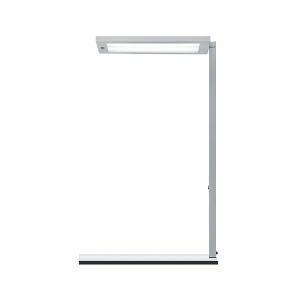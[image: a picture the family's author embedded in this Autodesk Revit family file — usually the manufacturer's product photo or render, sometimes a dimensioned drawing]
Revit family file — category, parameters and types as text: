
# Revit family: lavigo_core_-_dpt_9000_840_r_g1_srmet_00812479_ce18
name_source: partatom
category: Lighting Fixtures
units: mm (PartAtom-declared; Revit-internal decimal feet)

## family parameters
Cut with Voids When Loaded = No
Host = Face
Light Source = No
Part Type = Normal
Room Calculation Point = No
Round Connector Dimension = Use Diameter
Shared = No

## types (1)
- LAVIGO.core - DPT 9000/840/R/G1/SRMET (1 x LED, 8900 lm, 4000K)
    Apparent Load = 62 VA
    Approval mark = CE
    CIE Flux Codes = 59 88 97 35 100
    Color Rendering = 80-89
    Color Temperature = 4000K
    Control Gear = Electronic ballast
    Default Elevation = 1800 mm
    Description = DPT 9000/840/R/G1|Desk-mounted luminaire|light source: LED Cold white   |work equipment: Electronic ballast DALI|connected load: 220-240 V, 50/60 Hz|Power consumption: approx. 62 W|standby: approx. 0,30|power factor: approx. 0,959|luminous flux: 8900 lm|luminous efficacy: 143 lm/W|light distribution: Direct/indirect|direct ratio: approx. 35 %|color rendering index (CRI): >= 80|chromaticity tolerance:  3 SDCM|technology: Presence and daylight sensor control (PIR)|operation: Rocker switch|luminaire body|material: Steel/plastic|surface: Painted|colour: Silver metallic|lamp cover: Polycarbonate (PC), Clear|tubular section|material: Steel tube|surface: Painted|Form: Tubular section upright|colour of tubular section: Silver metallic|weight (net): approx. 8.3 kg|mains lead: 3.70 m Mains plug CEE 7/VII|Fastening: Socket, Table adaptor|decorative contrast side parts: Metallic silver|glare control: Prism aperture|luminance(L65): <= 4400 cd/m|unified glare rating(4H 8H): <=  16|special features: Luminaire head detachable, Direct and indirect light switchable together, Flicker-free, Integrated light and presence sensor PIR, Motion sensor time-out of 15mins~|
    Frequency = 50 Hz, 60 Hz
    Height = 36 mm
    Lamp = 1 x LED
    Lamp Light Flux = 8900 lm
    Lamp count = 1
    Length = 675 mm
    Luminous efficacy = 144 lm/W
    Manufacturer = Waldmann
    ModVariant = No
    Model = 00812479
    Mounting Place = Floor
    Mounting Type = Freestanding
    Number of Poles = 1
    OnlyDefault = Yes
    Power Factor = 1
    Product Name = LAVIGO.core - DPT 9000/840/R/G1/SRMET
    Product group = Desk mounted luminaire with detector
    ProductGroupID = 2201
    Protection Class = Protection class I
    Protection Degree = IP 20
    RLX_Detail_Level = 1
    RLX_Emergency_Light_Flux = 0 lm
    RLX_Emergency_Type = 0
    RLX_Emergency_Type_DB = No
    RlxData = <blob elided: 31269 chars, md5=5b0912f4>
    Socket = socket
    Standby Power = 0 W
    System Light Flux = 8900 lm
    System Power = 62 W
    Type Comments = Product without accessories
    Type Image = 121808000-00758533.jpg
    URL = http://relux.com
    VarID = ---
    Voltage = 230 V
    Voltage Range = 220-240 V
    Weight = 0.00 kg
    Width = 320 mm

## geometry (parser evidence)
native form markers: Blend x4, Sweep x17
no freeform markers — native parametric forms only
